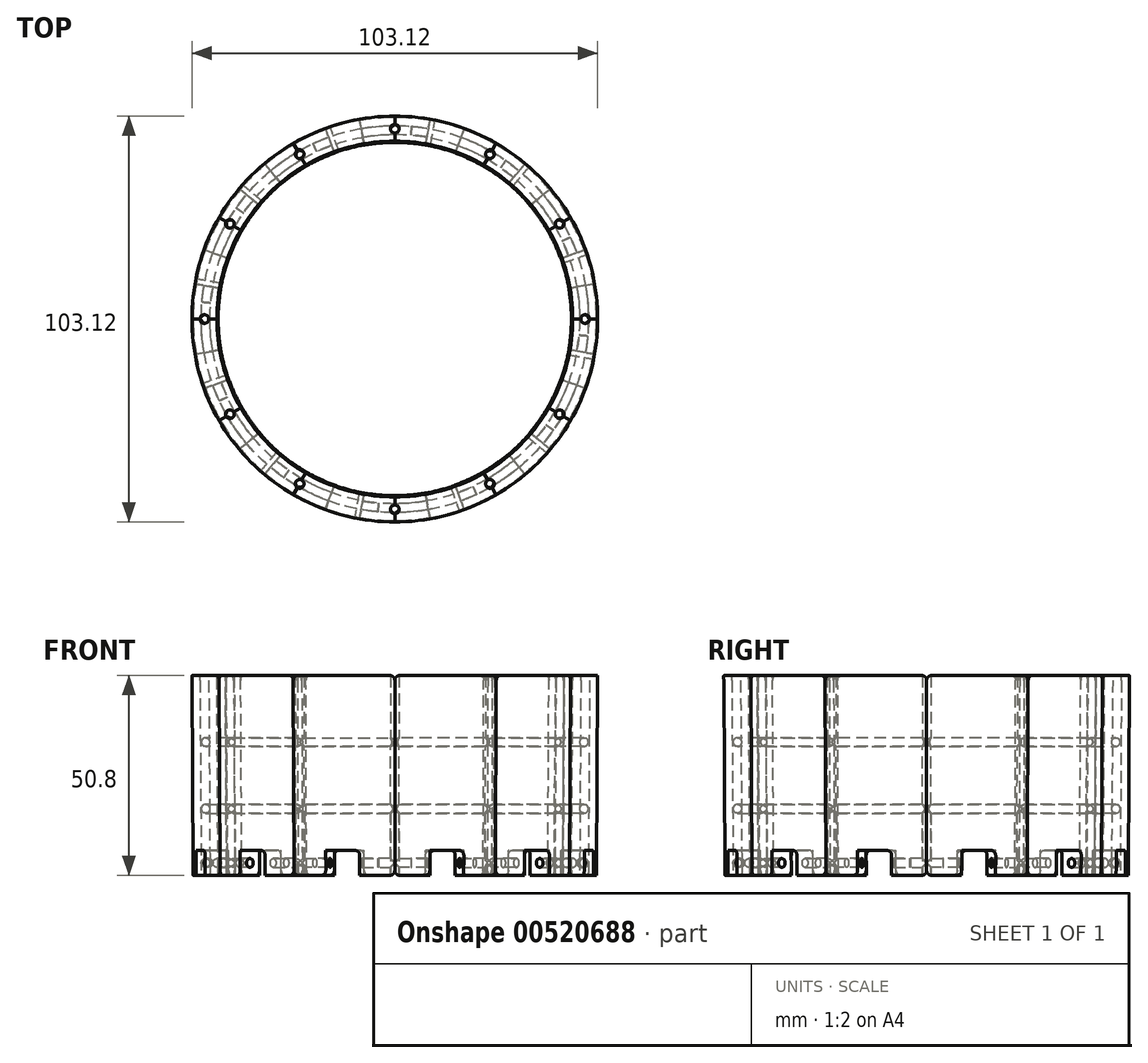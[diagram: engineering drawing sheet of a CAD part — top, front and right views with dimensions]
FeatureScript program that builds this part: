
annotation { "Feature Type Name" : "Feature", "Feature Type Description" : "" }
export const myFeature = defineFeature(function(context is Context, id is Id, definition is map)
    precondition{}
    {
        {
            var Q0;
            Q0=qCreatedBy(makeId("Front.planeOp"),FACE);
            var sketch = newSketch(context, id + "F0", { "sketchPlane" : qUnion([Q0])});
            skLineSegment(sketch, "E0", {"start": v(0, 0) * mm, "end": v(0, 50.8) * mm});
            skLineSegment(sketch, "E1", {"start": v(0, 50.8) * mm, "end": v(51.56, 50.8) * mm});
            skLineSegment(sketch, "E2", {"start": v(0, 0) * mm, "end": v(51.23, 0) * mm});
            skLineSegment(sketch, "E3", {"start": v(51.23, 0) * mm, "end": v(51.56, 50.8) * mm});
            skSolve(sketch);
        }
        {
            var Q0;
            Q0=makeQuery(id+"F0.imprint","IMPRINT",FACE,{"disambiguationData":[TD([[makeQuery(id+"F0.imprint","IMPRINT",EDGE,{"derivedFrom":sQuery(id+"F0.wireOp",EDGE,"E0")}),-1.0]])]});
            var Q1;
            Q1=sQuery(id+"F0.wireOp",EDGE,"E0");
            revolve(context, id + "F1", {"entities" : qUnion([Q0]), "axis" : qUnion([Q1]), "revolveType" : RevolveType.ONE_DIRECTION, "angle" : 30 * degree});
        }
        {
            var Q0;
            Q0=makeQuery(id+"F1.opRevolve","CAP_FACE",FACE,{"disambiguationData":[OSD([sQuery(id+"F0.wireOp",EDGE,"E0"),sQuery(id+"F0.wireOp",EDGE,"E1"),sQuery(id+"F0.wireOp",EDGE,"E2"),sQuery(id+"F0.wireOp",EDGE,"E3")])],"isStart":true});
            var sketch = newSketch(context, id + "F2", { "sketchPlane" : qUnion([Q0])});
            skLineSegment(sketch, "E4", {"start": v(0, 50.8) * mm, "end": v(0, 0) * mm});
            skLineSegment(sketch, "E5", {"start": v(0, 0) * mm, "end": v(44.88, 0) * mm});
            skLineSegment(sketch, "E6", {"start": v(0, 50.8) * mm, "end": v(45.21, 50.8) * mm});
            skLineSegment(sketch, "E7", {"start": v(45.21, 50.8) * mm, "end": v(44.88, 0) * mm});
            skSolve(sketch);
        }
        {
            var Q0;
            Q0 = qSketchRegion(id + "F2", true);
            var Q1;
            Q1=sQuery(id+"F2.wireOp",EDGE,"E4");
            revolve(context, id + "F3", {"operationType" : NewBodyOperationType.REMOVE, "entities" : qUnion([Q0]), "axis" : qUnion([Q1]), "revolveType" : RevolveType.FULL, "oppositeDirection" : true});
        }
        {
            var Q0;
            Q0=makeQuery(id+"F1.opRevolve","CAP_FACE",FACE,{"disambiguationData":[OSD([sQuery(id+"F0.wireOp",EDGE,"E0"),sQuery(id+"F0.wireOp",EDGE,"E1"),sQuery(id+"F0.wireOp",EDGE,"E2"),sQuery(id+"F0.wireOp",EDGE,"E3")])],"isStart":true});
            var sketch = newSketch(context, id + "F4", { "sketchPlane" : qUnion([Q0])});
            skLineSegment(sketch, "E8", {"start": v(0, 0) * mm, "end": v(51.23, 0) * mm, "construction": true});
            skLineSegment(sketch, "E9", {"start": v(51.23, 0) * mm, "end": v(51.27, 6.35) * mm});
            skLineSegment(sketch, "E10", {"start": v(51.27, 6.35) * mm, "end": v(44.92, 6.4) * mm});
            skLineSegment(sketch, "E11", {"start": v(44.92, 6.4) * mm, "end": v(44.88, 0) * mm});
            skLineSegment(sketch, "E12", {"start": v(44.88, 0) * mm, "end": v(51.23, 0) * mm});
            skLineSegment(sketch, "E13", {"start": v(0, -1.63) * mm, "end": v(0, 22.61) * mm, "construction": true});
            skSolve(sketch);
        }
        {
            var Q0;
            Q0 = qSketchRegion(id + "F4", true);
            var Q1;
            Q1=sQuery(id+"F4.wireOp",EDGE,"E13");
            revolve(context, id + "F5", {"operationType" : NewBodyOperationType.REMOVE, "entities" : qUnion([Q0]), "axis" : qUnion([Q1]), "revolveType" : RevolveType.ONE_DIRECTION, "angle" : 20 * degree});
        }
        {
            var Q0;
            Q0 = qSketchRegion(id + "F4", true);
            var Q1;
            Q1=sQuery(id+"F4.wireOp",EDGE,"E13");
            revolve(context, id + "F6", {"operationType" : NewBodyOperationType.ADD, "entities" : qUnion([Q0]), "axis" : qUnion([Q1]), "revolveType" : RevolveType.ONE_DIRECTION, "angle" : 10 * degree});
        }
        {
            var Q0;
            Q0=makeQuery(id+"F6.boolean.opBoolean","MERGE",FACE,{"derivedFrom":[makeQuery(id+"F1.opRevolve","CAP_FACE",FACE,{"disambiguationData":[OSD([sQuery(id+"F0.wireOp",EDGE,"E0"),sQuery(id+"F0.wireOp",EDGE,"E1"),sQuery(id+"F0.wireOp",EDGE,"E2"),sQuery(id+"F0.wireOp",EDGE,"E3")])],"isStart":true}),makeQuery(id+"F6.opRevolve","CAP_FACE",FACE,{"disambiguationData":[OSD([sQuery(id+"F4.wireOp",EDGE,"E9"),sQuery(id+"F4.wireOp",EDGE,"E10"),sQuery(id+"F4.wireOp",EDGE,"E11"),sQuery(id+"F4.wireOp",EDGE,"E12")])],"isStart":true})]});
            var sketch = newSketch(context, id + "F7", { "sketchPlane" : qUnion([Q0])});
            skLineSegment(sketch, "E14", {"start": v(0, 0) * mm, "end": v(0, 25.16) * mm, "construction": true});
            skLineSegment(sketch, "E15", {"start": v(45.21, 50.8) * mm, "end": v(48.39, 50.8) * mm, "construction": true});
            skLineSegment(sketch, "E16", {"start": v(44.88, 0) * mm, "end": v(48.06, 0) * mm, "construction": true});
            skLineSegment(sketch, "E17", {"start": v(48.06, 0) * mm, "end": v(48.08, 4.3) * mm, "construction": true});
            skPoint(sketch, "E18", {"position": v(48.08, 3.17) * mm});
            skCircle(sketch, "E19", {"center": v(48.08, 3.17) * mm, "radius": 1.12 * mm, "construction": true});
            skLineSegment(sketch, "E20", {"start": v(0, 0) * mm, "end": v(48.06, 0) * mm, "construction": true});
            skLineSegment(sketch, "E21", {"start": v(48.06, 0) * mm, "end": v(48.06, 16.93) * mm, "construction": true});
            skLineSegment(sketch, "E22", {"start": v(48.06, 16.93) * mm, "end": v(48.06, 33.87) * mm, "construction": true});
            skCircle(sketch, "E23", {"center": v(48.06, 33.87) * mm, "radius": 1.12 * mm});
            skCircle(sketch, "E24", {"center": v(48.06, 16.93) * mm, "radius": 1.12 * mm});
            skSolve(sketch);
        }
        {
            var Q0;
            Q0 = qSketchRegion(id + "F7", true);
            var Q1;
            Q1=sQuery(id+"F7.wireOp",EDGE,"E14");
            revolve(context, id + "F8", {"operationType" : NewBodyOperationType.REMOVE, "entities" : qUnion([Q0]), "axis" : qUnion([Q1]), "revolveType" : RevolveType.FULL, "oppositeDirection" : true});
        }
        {
            var Q0;
            Q0=makeQuery(id+"F6.opRevolve","SWEPT_FACE",FACE,{"disambiguationData":[OSD([sQuery(id+"F4.wireOp",EDGE,"E12")])]});
            var sketch = newSketch(context, id + "F9", { "sketchPlane" : qUnion([Q0])});
            skLineSegment(sketch, "E25", {"start": v(51.23, 0) * mm, "end": v(48.06, 0) * mm, "construction": true});
            skCircle(sketch, "E26", {"center": v(48.06, 0) * mm, "radius": 1.11 * mm});
            skSolve(sketch);
        }
        {
            var Q0;
            Q0=makeQuery(id+"F1.opRevolve","SWEPT_FACE",FACE,{"disambiguationData":[OSD([sQuery(id+"F0.wireOp",EDGE,"E1")])]});
            var sketch = newSketch(context, id + "F10", { "sketchPlane" : qUnion([Q0])});
            skLineSegment(sketch, "E27", {"start": v(51.56, 0) * mm, "end": v(48.39, 0) * mm, "construction": true});
            skCircle(sketch, "E28", {"center": v(48.39, 0) * mm, "radius": 1.11 * mm});
            skSolve(sketch);
        }
        {
            var Q0;
            Q0=makeQuery(id+"F1.opRevolve","SWEPT_FACE",FACE,{"disambiguationData":[OSD([sQuery(id+"F0.wireOp",EDGE,"E2")])]});
            var sketch = newSketch(context, id + "F11", { "sketchPlane" : qUnion([Q0])});
            skLineSegment(sketch, "E29", {"start": v(44.37, -25.62) * mm, "end": v(41.62, -24.03) * mm, "construction": true});
            skCircle(sketch, "E30", {"center": v(41.62, -24.03) * mm, "radius": 1.11 * mm});
            skSolve(sketch);
        }
        {
            var Q0;
            Q0=makeQuery(id+"F1.opRevolve","SWEPT_FACE",FACE,{"disambiguationData":[OSD([sQuery(id+"F0.wireOp",EDGE,"E1")])]});
            var sketch = newSketch(context, id + "F12", { "sketchPlane" : qUnion([Q0])});
            skLineSegment(sketch, "E31", {"start": v(44.65, 25.78) * mm, "end": v(41.9, 24.2) * mm, "construction": true});
            skCircle(sketch, "E32", {"center": v(41.9, 24.2) * mm, "radius": 1.11 * mm});
            skSolve(sketch);
        }
        {
            var Q0;
            Q0=makeQuery(id+"F5.boolean.opBoolean","COPY",EDGE,{"derivedFrom":makeQuery(id+"F5.opRevolve","CAP_EDGE",EDGE,{"disambiguationData":[OSD([sQuery(id+"F4.wireOp",EDGE,"E10")])],"isStart":false})});
            var Q1;
            Q1=makeQuery(id+"F5.boolean.opBoolean","COPY",EDGE,{"derivedFrom":makeQuery(id+"F5.opRevolve","CAP_EDGE",EDGE,{"disambiguationData":[OSD([sQuery(id+"F4.wireOp",EDGE,"E12")])],"isStart":false})});
            var Q2;
            Q2=makeQuery(id+"F6.opRevolve","CAP_EDGE",EDGE,{"disambiguationData":[OSD([sQuery(id+"F4.wireOp",EDGE,"E12")])],"isStart":false});
            var Q3;
            Q3=makeQuery(id+"F6.opRevolve","CAP_EDGE",EDGE,{"disambiguationData":[OSD([sQuery(id+"F4.wireOp",EDGE,"E10")])],"isStart":false});
            var Q4;
            Q4=makeQuery(id+"F1.opRevolve","CAP_EDGE",EDGE,{"disambiguationData":[OSD([sQuery(id+"F0.wireOp",EDGE,"E2")])],"isStart":false});
            var Q5;
            Q5=makeQuery(id+"F6.opRevolve","CAP_EDGE",EDGE,{"disambiguationData":[OSD([sQuery(id+"F4.wireOp",EDGE,"E12")])],"isStart":true});
            var Q6;
            Q6=makeQuery(id+"F1.opRevolve","CAP_EDGE",EDGE,{"disambiguationData":[OSD([sQuery(id+"F0.wireOp",EDGE,"E1")])],"isStart":true});
            var Q7;
            Q7=makeQuery(id+"F1.opRevolve","CAP_EDGE",EDGE,{"disambiguationData":[OSD([sQuery(id+"F0.wireOp",EDGE,"E1")])],"isStart":false});
            fillet(context, id + "F13", {"entities" : qUnion([Q0, Q1, Q2, Q3, Q4, Q5, Q6, Q7]), "radius" : 1.27 * mm, "tangentPropagation" : true, "allowEdgeOverflow" : false});
        }
        {
            var Q0;
            Q0=qCreatedBy(makeId("Front.planeOp"),FACE);
            var sketch = newSketch(context, id + "F14", { "sketchPlane" : qUnion([Q0])});
            skLineSegment(sketch, "E33", {"start": v(0, 0) * mm, "end": v(48.06, 0) * mm, "construction": true});
            skLineSegment(sketch, "E34", {"start": v(48.06, 0) * mm, "end": v(48.06, 3.18) * mm, "construction": true});
            skCircle(sketch, "E35", {"center": v(48.06, 3.18) * mm, "radius": 1.12 * mm});
            skSolve(sketch);
        }
        {
            var Q0;
            Q0 = qSketchRegion(id + "F14", true);
            var Q1;
            Q1=sQuery(id+"F7.wireOp",EDGE,"E14");
            revolve(context, id + "F15", {"operationType" : NewBodyOperationType.REMOVE, "entities" : qUnion([Q0]), "axis" : qUnion([Q1]), "revolveType" : RevolveType.ONE_DIRECTION, "angle" : 25 * degree});
        }
        {
            var Q1;
            {var subQ0=sQuery(id+"F10.wireOp",EDGE,"E28");var subQ1=makeQuery(id+"F1.opRevolve","CAP_EDGE",EDGE,{"disambiguationData":[OSD([sQuery(id+"F0.wireOp",EDGE,"E1")])],"isStart":true});var subQ2=makeQuery(id+"F10.imprint","INTERSECT",VERTEX,{"disambiguationData":[OD(0.0)],"derivedFrom":[subQ1,subQ0]});Q1=makeQuery(id+"F10.imprint","IMPRINT",FACE,{"disambiguationData":[TD([[makeQuery(id+"F10.imprint","IMPRINT",EDGE,{"disambiguationData":[TD([[subQ2,-1.0]])],"derivedFrom":subQ0}),1.0]])]});}
            var Q2;
            {var subQ0=sQuery(id+"F9.wireOp",EDGE,"E26");var subQ1=makeQuery(id+"F6.opRevolve","CAP_EDGE",EDGE,{"disambiguationData":[OSD([sQuery(id+"F4.wireOp",EDGE,"E12")])],"isStart":true});var subQ2=makeQuery(id+"F9.imprint","INTERSECT",VERTEX,{"disambiguationData":[OD(0.0)],"derivedFrom":[subQ1,subQ0]});Q2=makeQuery(id+"F9.imprint","IMPRINT",FACE,{"disambiguationData":[TD([[makeQuery(id+"F9.imprint","IMPRINT",EDGE,{"disambiguationData":[TD([[subQ2,1.0]])],"derivedFrom":subQ0}),1.0]])]});}
            loft(context, id + "F16", {"operationType" : NewBodyOperationType.REMOVE, "sheetProfilesArray" : [{ "sheetProfileEntities" : qUnion([Q1]) }, { "sheetProfileEntities" : qUnion([Q2]) }]});
        }
        {
            var Q1;
            {var subQ0=sQuery(id+"F12.wireOp",EDGE,"E32");var subQ1=makeQuery(id+"F1.opRevolve","CAP_EDGE",EDGE,{"disambiguationData":[OSD([sQuery(id+"F0.wireOp",EDGE,"E1")])],"isStart":false});var subQ2=makeQuery(id+"F12.imprint","INTERSECT",VERTEX,{"disambiguationData":[OD(0.0)],"derivedFrom":[subQ1,subQ0]});Q1=makeQuery(id+"F12.imprint","IMPRINT",FACE,{"disambiguationData":[TD([[makeQuery(id+"F12.imprint","IMPRINT",EDGE,{"disambiguationData":[TD([[subQ2,1.0]])],"derivedFrom":subQ0}),1.0]])]});}
            var Q2;
            {var subQ0=sQuery(id+"F11.wireOp",EDGE,"E30");var subQ1=makeQuery(id+"F1.opRevolve","CAP_EDGE",EDGE,{"disambiguationData":[OSD([sQuery(id+"F0.wireOp",EDGE,"E2")])],"isStart":false});var subQ2=makeQuery(id+"F11.imprint","INTERSECT",VERTEX,{"disambiguationData":[OD(0.0)],"derivedFrom":[subQ1,subQ0]});Q2=makeQuery(id+"F11.imprint","IMPRINT",FACE,{"disambiguationData":[TD([[makeQuery(id+"F11.imprint","IMPRINT",EDGE,{"disambiguationData":[TD([[subQ2,-1.0]])],"derivedFrom":subQ0}),1.0]])]});}
            loft(context, id + "F17", {"operationType" : NewBodyOperationType.REMOVE, "sheetProfilesArray" : [{ "sheetProfileEntities" : qUnion([Q1]) }, { "sheetProfileEntities" : qUnion([Q2]) }]});
        }
        {
            var Q0;
            Q0=makeQuery(id+"F1.opRevolve","SWEPT_BODY",BODY,{"disambiguationData":[OSD([sQuery(id+"F0.wireOp",EDGE,"E0"),sQuery(id+"F0.wireOp",EDGE,"E1"),sQuery(id+"F0.wireOp",EDGE,"E2"),sQuery(id+"F0.wireOp",EDGE,"E3")])]});
            var Q1;
            Q1=sQuery(id+"F2.wireOp",EDGE,"E4");
            circularPattern(context, id + "F18", {"entities" : qUnion([Q0]), "axis" : qUnion([Q1]), "angle" : 360 * degree, "instanceCount" : 12, "equalSpace" : true});
        }
    });
